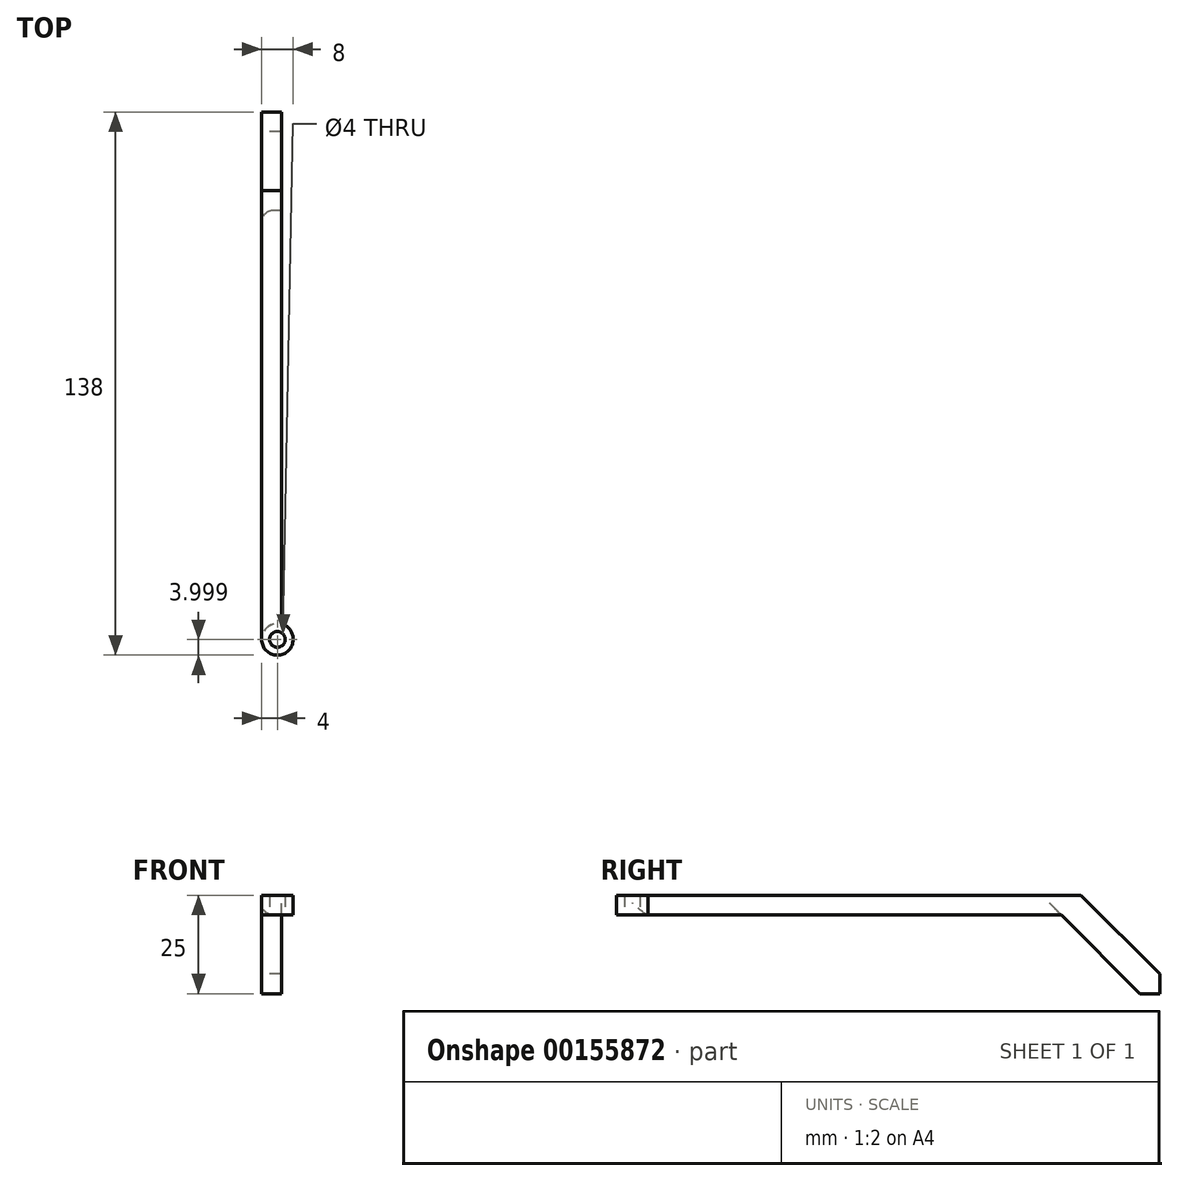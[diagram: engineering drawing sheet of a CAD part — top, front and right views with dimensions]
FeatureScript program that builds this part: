
annotation { "Feature Type Name" : "Feature", "Feature Type Description" : "" }
export const myFeature = defineFeature(function(context is Context, id is Id, definition is map)
    precondition{}
    {
        {
            var Q0;
            Q0=qCreatedBy(makeId("Right.planeOp"),FACE);
            var sketch = newSketch(context, id + "F0", { "sketchPlane" : qUnion([Q0])});
            skLineSegment(sketch, "E0", {"start": v(-112.32, 21.42) * mm, "end": v(-7.32, 21.42) * mm});
            skLineSegment(sketch, "E1.bottom", {"start": v(-7.32, 21.42) * mm, "end": v(17.68, 21.42) * mm});
            skLineSegment(sketch, "E1.top", {"start": v(-7.32, -3.58) * mm, "end": v(17.68, -3.58) * mm});
            skLineSegment(sketch, "E1.left", {"start": v(-7.32, 21.42) * mm, "end": v(-7.32, -3.58) * mm});
            skLineSegment(sketch, "E1.right", {"start": v(17.68, 21.42) * mm, "end": v(17.68, -3.58) * mm});
            skLineSegment(sketch, "E2", {"start": v(-112.32, 16.42) * mm, "end": v(-7.32, 16.42) * mm});
            skLineSegment(sketch, "E3", {"start": v(-7.32, 16.42) * mm, "end": v(12.68, -3.58) * mm});
            skLineSegment(sketch, "E4", {"start": v(12.68, -3.58) * mm, "end": v(17.68, 1.42) * mm});
            skLineSegment(sketch, "E5", {"start": v(17.68, 1.42) * mm, "end": v(-2.32, 21.42) * mm});
            skLineSegment(sketch, "E6", {"start": v(-112.32, 16.42) * mm, "end": v(-112.32, 21.42) * mm});
            skSolve(sketch);
        }
        {
            var Q0;
            {var subQ0=sQuery(id+"F0.wireOp",EDGE,"E0");Q0=makeQuery(id+"F0.imprint","IMPRINT",FACE,{"disambiguationData":[TD([[makeQuery(id+"F0.imprint","IMPRINT",EDGE,{"derivedFrom":subQ0}),-1.0]])]});}
            var Q1;
            {var subQ0=sQuery(id+"F0.wireOp",EDGE,"E3");Q1=makeQuery(id+"F0.imprint","IMPRINT",FACE,{"disambiguationData":[TD([[makeQuery(id+"F0.imprint","IMPRINT",EDGE,{"derivedFrom":subQ0}),1.0]])]});}
            var Q2;
            {var subQ3=sQuery(id+"F0.wireOp",EDGE,"E4");Q2=makeQuery(id+"F0.imprint","IMPRINT",FACE,{"disambiguationData":[TD([[makeQuery(id+"F0.imprint","IMPRINT",EDGE,{"derivedFrom":subQ3}),-1.0]])]});}
            extrude(context, id + "F1", {"entities" : qUnion([Q0, Q1, Q2]), "depth" : 5 * mm});
        }
        {
            var Q0;
            Q0=makeQuery(id+"F4.boolean.opBoolean","MERGE",EDGE,{"derivedFrom":[makeQuery(id+"F1.opExtrude","CAP_EDGE",EDGE,{"disambiguationData":[OSD([sQuery(id+"F0.wireOp",EDGE,"E2")])],"isStart":true}),makeQuery(id+"F4.opExtrude","CAP_EDGE",EDGE,{"disambiguationData":[OSD([sQuery(id+"F3.wireOp",EDGE,"E8.left")])],"isStart":true})]});
            fillet(context, id + "F2", {"entities" : qUnion([Q0]), "radius" : 3 * mm, "allowEdgeOverflow" : false});
        }
        {
            var Q0;
            Q0=makeQuery(id+"F1.opExtrude","SWEPT_FACE",FACE,{"disambiguationData":[OSD([sQuery(id+"F0.wireOp",EDGE,"E2")])]});
            var sketch = newSketch(context, id + "F3", { "sketchPlane" : qUnion([Q0])});
            skPoint(sketch, "E7.0", {"position": v(0, 112.32) * mm});
            skLineSegment(sketch, "E8.bottom", {"start": v(0, 112.32) * mm, "end": v(8, 112.32) * mm});
            skLineSegment(sketch, "E8.top", {"start": v(0, 120.32) * mm, "end": v(8, 120.32) * mm});
            skLineSegment(sketch, "E8.left", {"start": v(0, 112.32) * mm, "end": v(0, 120.32) * mm});
            skLineSegment(sketch, "E8.right", {"start": v(8, 112.32) * mm, "end": v(8, 120.32) * mm});
            skCircle(sketch, "E9", {"center": v(4, 116.32) * mm, "radius": 2 * mm});
            skPoint(sketch, "E9.centerSnap0", {"position": v(4, 120.32) * mm});
            skPoint(sketch, "E9.centerSnap1", {"position": v(0, 116.32) * mm});
            skSolve(sketch);
        }
        {
            var Q0;
            Q0 = qSketchRegion(id + "F3", true);
            extrude(context, id + "F4", {"entities" : qUnion([Q0]), "operationType" : NewBodyOperationType.ADD, "oppositeDirection" : true, "depth" : 5 * mm});
        }
        {
            var Q0;
            Q0=makeQuery(id+"F4.opExtrude","SWEPT_EDGE",EDGE,{"disambiguationData":[OSD([sQuery(id+"F3.wireOp",EDGE,"E8.bottom"),sQuery(id+"F3.wireOp",EDGE,"E8.right")])]});
            var Q1;
            Q1=makeQuery(id+"F4.opExtrude","SWEPT_EDGE",EDGE,{"disambiguationData":[OSD([sQuery(id+"F3.wireOp",EDGE,"E8.top"),sQuery(id+"F3.wireOp",EDGE,"E8.right")])]});
            var Q2;
            Q2=makeQuery(id+"F4.opExtrude","SWEPT_EDGE",EDGE,{"disambiguationData":[OSD([sQuery(id+"F3.wireOp",EDGE,"E8.top"),sQuery(id+"F3.wireOp",EDGE,"E8.left")])]});
            var Q3;
            Q3=makeQuery(id+"F4.opExtrude","SWEPT_EDGE",EDGE,{"disambiguationData":[OSD([sQuery(id+"F3.wireOp",EDGE,"E8.bottom"),sQuery(id+"F3.wireOp",EDGE,"E8.left")])]});
            fillet(context, id + "F5", {"entities" : qUnion([Q0, Q1, Q2, Q3]), "radius" : 4 * mm, "tangentPropagation" : true, "allowEdgeOverflow" : false});
        }
    });
